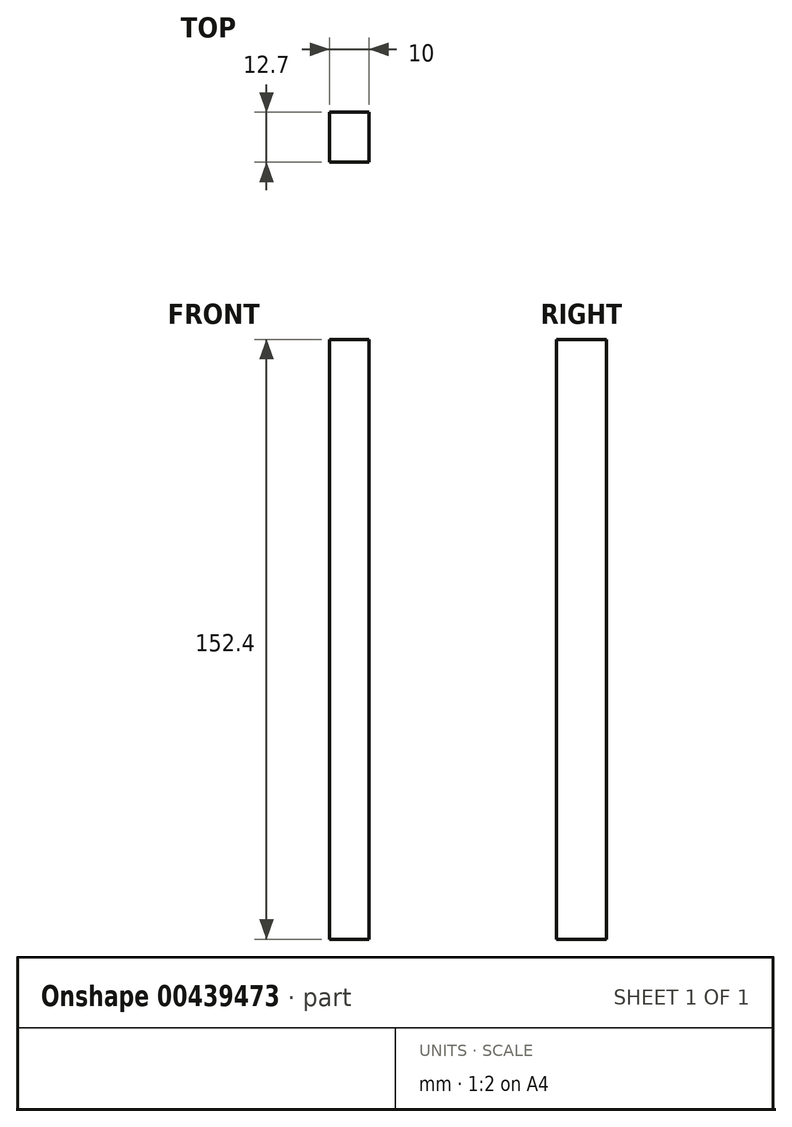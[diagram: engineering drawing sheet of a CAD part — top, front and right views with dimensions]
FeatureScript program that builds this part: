
annotation { "Feature Type Name" : "Feature", "Feature Type Description" : "" }
export const myFeature = defineFeature(function(context is Context, id is Id, definition is map)
    precondition{}
    {
        {
            var Q0;
            Q0=qCreatedBy(makeId("Front.planeOp"),FACE);
            var sketch = newSketch(context, id + "F0", { "sketchPlane" : qUnion([Q0])});
            skLineSegment(sketch, "E0.bottom", {"start": v(-5, 76.2) * mm, "end": v(5, 76.2) * mm});
            skLineSegment(sketch, "E0.top", {"start": v(-5, -76.2) * mm, "end": v(5, -76.2) * mm});
            skLineSegment(sketch, "E0.left", {"start": v(-5, 76.2) * mm, "end": v(-5, -76.2) * mm});
            skLineSegment(sketch, "E0.right", {"start": v(5, 76.2) * mm, "end": v(5, -76.2) * mm});
            skPoint(sketch, "E0.middle", {"position": v(0, 0) * mm});
            skSolve(sketch);
        }
        {
            var Q0;
            Q0 = qSketchRegion(id + "F0", true);
            extrude(context, id + "F1", {"entities" : qUnion([Q0]), "depth" : 12.7 * mm});
        }
    });
